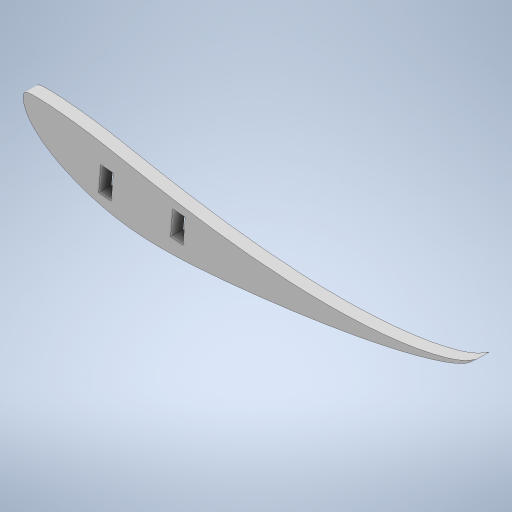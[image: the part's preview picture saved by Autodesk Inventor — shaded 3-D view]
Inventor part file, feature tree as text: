
AUTODESK INVENTOR PART (.ipt)
format: ipt  version: 2024 (Build 280153000, 153)  size: 299,008 bytes
history: native  units: mm
features: extrude x1, sketch x1
ambient origin geometry x8: Origin, YZ Plane, XZ Plane, XY Plane, X Axis, Y Axis, Z Axis, Center Point
bodies: Solid1 (feature_tree)
feature tree (2):
  extrude  "Extrusion1"  Depth=5.0mm
  sketch  "Sketch2"  dims[d0=5.0mm d1=0.0mm d2=0.5mm d3=0.872665mm d4=0.5mm d5=0.872665mm]
